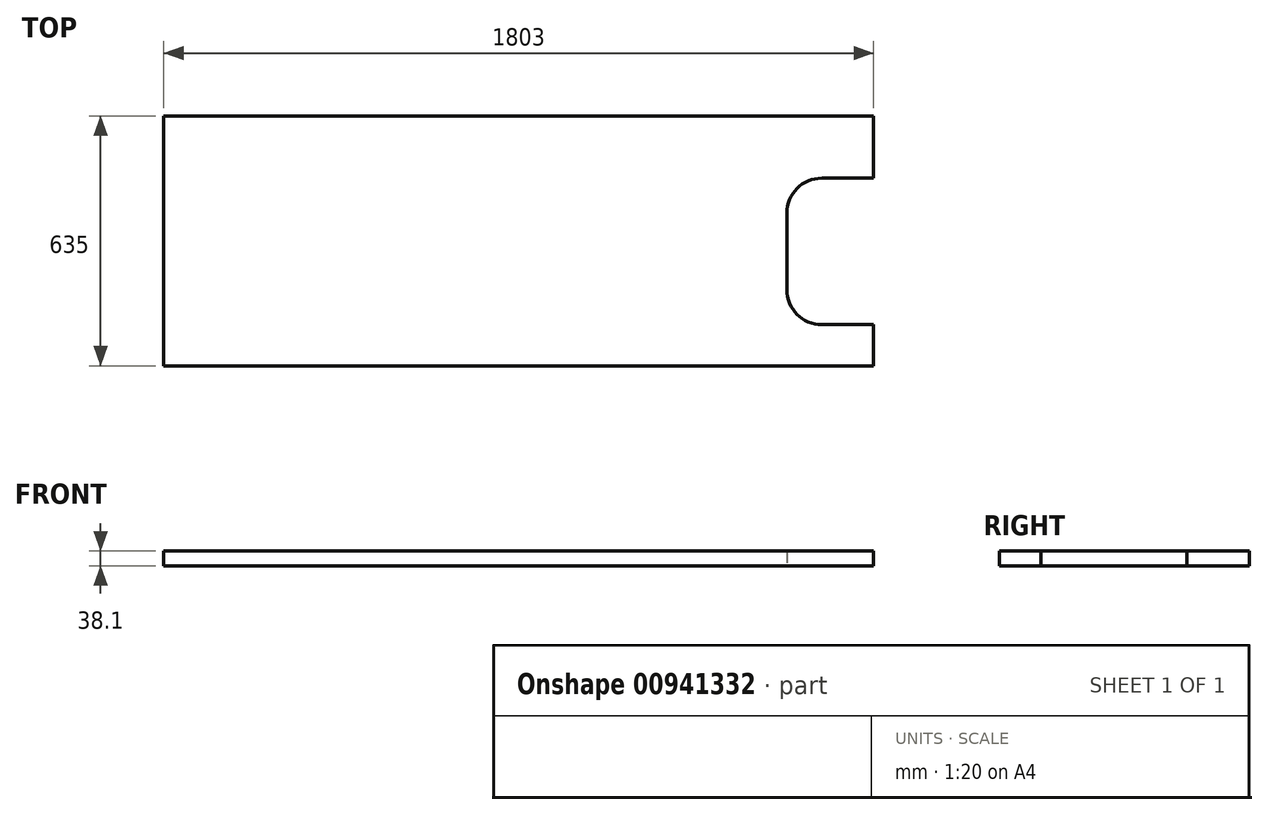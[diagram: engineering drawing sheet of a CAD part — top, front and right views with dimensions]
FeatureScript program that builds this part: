
annotation { "Feature Type Name" : "Feature", "Feature Type Description" : "" }
export const myFeature = defineFeature(function(context is Context, id is Id, definition is map)
    precondition{}
    {
        {
            var Q0;
            Q0=qCreatedBy(makeId("Right.planeOp"),FACE);
            var sketch = newSketch(context, id + "F0", { "sketchPlane" : qUnion([Q0])});
            skLineSegment(sketch, "E0.bottom", {"start": v(0, 0) * mm, "end": v(635, 0) * mm});
            skLineSegment(sketch, "E0.top", {"start": v(0, 38.1) * mm, "end": v(635, 38.1) * mm});
            skLineSegment(sketch, "E0.left", {"start": v(0, 0) * mm, "end": v(0, 38.1) * mm});
            skLineSegment(sketch, "E0.right", {"start": v(635, 0) * mm, "end": v(635, 38.1) * mm});
            skPoint(sketch, "E1.visualSharp", {"position": v(635, 38.1) * mm});
            skArc(sketch, "E1.filletArc", {"start": v(635, 19.05) * mm, "mid": v(629.42, 32.52) * mm, "end": v(615.95, 38.1) * mm, "construction": true});
            skSolve(sketch);
        }
        {
            var Q0;
            Q0=makeQuery(id+"F0.imprint","IMPRINT",FACE,{"disambiguationData":[TD([[makeQuery(id+"F0.imprint","IMPRINT",EDGE,{"derivedFrom":sQuery(id+"F0.wireOp",EDGE,"E0.bottom")}),1.0]])]});
            extrude(context, id + "F1", {"entities" : qUnion([Q0]), "depth" : 1803 * mm, "offsetDistance" : 25 * mm});
        }
        {
            var Q0;
            Q0=qCreatedBy(makeId("Top.planeOp"),FACE);
            var sketch = newSketch(context, id + "F2", { "sketchPlane" : qUnion([Q0])});
            skLineSegment(sketch, "E2.0", {"start": v(1803, 0) * mm, "end": v(1803, 635) * mm, "construction": true});
            skLineSegment(sketch, "E3.bottom", {"start": v(1803, 477) * mm, "end": v(1583, 477) * mm});
            skLineSegment(sketch, "E3.top", {"start": v(1803, 105) * mm, "end": v(1583, 105) * mm});
            skLineSegment(sketch, "E3.left", {"start": v(1803, 477) * mm, "end": v(1803, 105) * mm});
            skLineSegment(sketch, "E3.right", {"start": v(1583, 477) * mm, "end": v(1583, 105) * mm});
            skSolve(sketch);
        }
        {
            var Q0;
            Q0 = qSketchRegion(id + "F2", true);
            extrude(context, id + "F3", {"entities" : qUnion([Q0]), "operationType" : NewBodyOperationType.REMOVE, "endBound" : BoundingType.THROUGH_ALL, "depth" : 25 * mm, "offsetDistance" : 25 * mm});
        }
        {
            var Q0;
            Q0=makeQuery(id+"F3.boolean.opBoolean","COPY",EDGE,{"derivedFrom":makeQuery(id+"F3.opExtrude","SWEPT_EDGE",EDGE,{"disambiguationData":[OSD([sQuery(id+"F2.wireOp",EDGE,"E3.bottom"),sQuery(id+"F2.wireOp",EDGE,"E3.right")])]})});
            var Q1;
            Q1=makeQuery(id+"F3.boolean.opBoolean","COPY",EDGE,{"derivedFrom":makeQuery(id+"F3.opExtrude","SWEPT_EDGE",EDGE,{"disambiguationData":[OSD([sQuery(id+"F2.wireOp",EDGE,"E3.top"),sQuery(id+"F2.wireOp",EDGE,"E3.right")])]})});
            fillet(context, id + "F4", {"entities" : qUnion([Q0, Q1]), "radius" : 88.9 * mm, "tangentPropagation" : true, "allowEdgeOverflow" : false});
        }
    });
